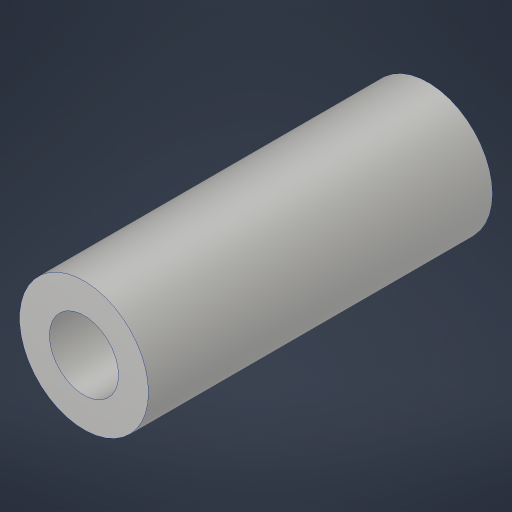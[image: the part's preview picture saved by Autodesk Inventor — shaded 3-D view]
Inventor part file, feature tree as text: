
AUTODESK INVENTOR PART (.ipt)
format: ipt  version: 2023.4 (Build 274418000, 418)  size: 171,008 bytes
history: native  units: in
note: dims shown in document units (in); Inventor stores cm internally (conversion verified against a paired STEP export)
features: extrude x1, hole x1
ambient origin geometry x8: Origin, YZ Plane, XZ Plane, XY Plane, X Axis, Y Axis, Z Axis, Center Point
bodies: Solid1 (feature_tree)
feature tree (2):
  extrude  "Extrusion1"  Depth=1.0in
  hole  "Hole1"  [1 undecoded]
note: 1 required parameter value undecoded (feature->parameter linkage not recoverable at this tier; creation-order binding heuristic only, values carry confidence <= 0.55)
